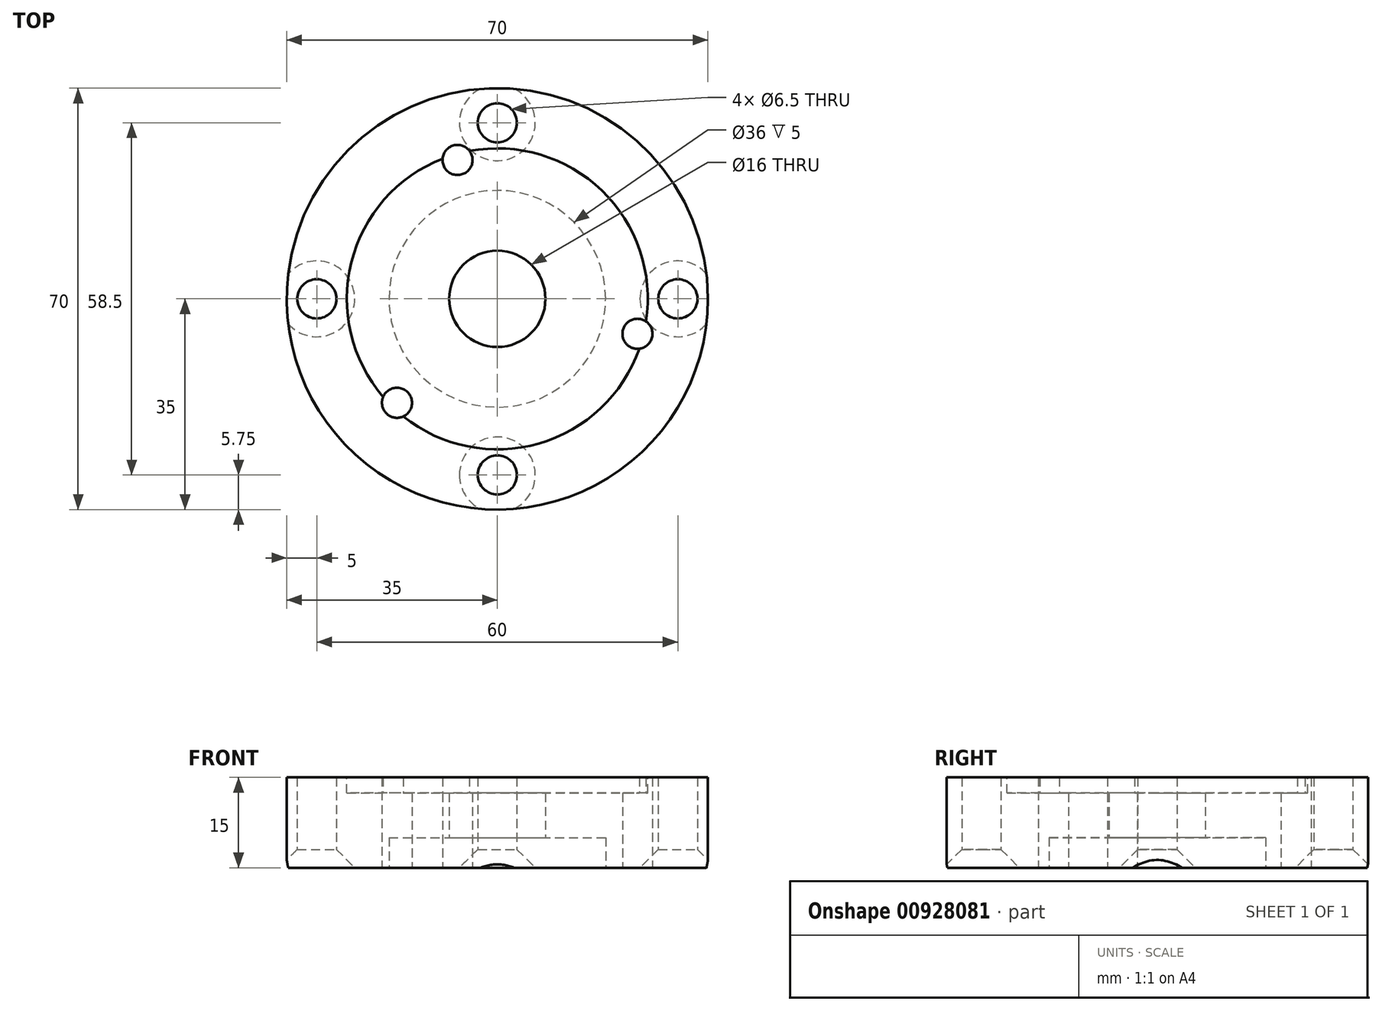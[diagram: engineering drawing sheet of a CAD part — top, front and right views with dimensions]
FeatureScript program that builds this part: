
annotation { "Feature Type Name" : "Feature", "Feature Type Description" : "" }
export const myFeature = defineFeature(function(context is Context, id is Id, definition is map)
    precondition{}
    {
        {
            var Q0;
            Q0=qCreatedBy(makeId("Top.planeOp"),FACE);
            var sketch = newSketch(context, id + "F0", { "sketchPlane" : qUnion([Q0])});
            skCircle(sketch, "E0", {"center": v(0, 0) * mm, "radius": 35 * mm});
            skSolve(sketch);
        }
        {
            var Q0;
            Q0=makeQuery(id+"F0.imprint","IMPRINT",FACE,{"disambiguationData":[TD([[makeQuery(id+"F0.imprint","IMPRINT",EDGE,{"derivedFrom":sQuery(id+"F0.wireOp",EDGE,"E0")}),1.0]])]});
            extrude(context, id + "F1", {"entities" : qUnion([Q0]), "depth" : 15 * mm, "offsetDistance" : 25 * mm});
        }
        {
            var Q0;
            Q0=makeQuery(id+"F1.opExtrude","CAP_FACE",FACE,{"disambiguationData":[OSD([sQuery(id+"F0.wireOp",EDGE,"E0")])],"isStart":false});
            var sketch = newSketch(context, id + "F2", { "sketchPlane" : qUnion([Q0])});
            skCircle(sketch, "E1", {"center": v(0, 0) * mm, "radius": 25 * mm});
            skSolve(sketch);
        }
        {
            var Q0;
            Q0=makeQuery(id+"F2.imprint","IMPRINT",FACE,{"disambiguationData":[TD([[makeQuery(id+"F2.imprint","IMPRINT",EDGE,{"derivedFrom":sQuery(id+"F2.wireOp",EDGE,"E1")}),1.0]])]});
            extrude(context, id + "F3", {"entities" : qUnion([Q0]), "operationType" : NewBodyOperationType.REMOVE, "oppositeDirection" : true, "depth" : 2.6 * mm, "offsetDistance" : 25 * mm});
        }
        {
            var Q0;
            Q0=makeQuery(id+"F1.opExtrude","CAP_FACE",FACE,{"disambiguationData":[OSD([sQuery(id+"F0.wireOp",EDGE,"E0")])],"isStart":true});
            var sketch = newSketch(context, id + "F4", { "sketchPlane" : qUnion([Q0])});
            skCircle(sketch, "E2", {"center": v(0, 0) * mm, "radius": 18 * mm});
            skCircle(sketch, "E3", {"center": v(0, 0) * mm, "radius": 29.25 * mm, "construction": true});
            skCircle(sketch, "E4", {"center": v(0, 0) * mm, "radius": 30 * mm, "construction": true});
            skPoint(sketch, "E5", {"position": v(0, -29.25) * mm});
            skPoint(sketch, "E6", {"position": v(0, 29.25) * mm});
            skPoint(sketch, "E7", {"position": v(30, 0) * mm});
            skPoint(sketch, "E8", {"position": v(-30, 0) * mm});
            skCircle(sketch, "E9", {"center": v(0, 0) * mm, "radius": 24 * mm, "construction": true});
            skPoint(sketch, "E10", {"position": v(-6.62, -23.07) * mm});
            skPoint(sketch, "E11.1.0", {"position": v(23.29, 5.8) * mm});
            skPoint(sketch, "E11.2.0", {"position": v(-16.67, 17.26) * mm});
            skSolve(sketch);
        }
        {
            var Q0;
            Q0=makeQuery(id+"F4.imprint","IMPRINT",FACE,{"disambiguationData":[TD([[makeQuery(id+"F4.imprint","IMPRINT",EDGE,{"derivedFrom":sQuery(id+"F4.wireOp",EDGE,"E2")}),1.0]])]});
            extrude(context, id + "F5", {"entities" : qUnion([Q0]), "operationType" : NewBodyOperationType.REMOVE, "oppositeDirection" : true, "depth" : 5 * mm, "offsetDistance" : 25 * mm});
        }
        {
            var Q0;
            Q0=sQuery(id+"F4.wireOp",VERTEX,"E10");
            var Q1;
            Q1=sQuery(id+"F4.wireOp",VERTEX,"E11.2.0");
            var Q2;
            Q2=sQuery(id+"F4.wireOp",VERTEX,"E11.1.0");
            var Q3;
            Q3=makeQuery(id+"F1.opExtrude","SWEPT_BODY",BODY,{"disambiguationData":[OSD([sQuery(id+"F0.wireOp",EDGE,"E0")])]});
            hole(context, id + "F6", {"style" : HoleStyle.SIMPLE, "endStyle" : HoleEndStyle.THROUGH, "standardTappedOrClearance" : lookupTablePath({ "standard" : "ISO", "engagement" : "75%", "pitch" : "1 mm", "size" : "M6", "type" : "Tapped" }), "standardBlindInLast" : lookupTablePath({ "standard" : "ISO", "engagement" : "75%", "pitch" : "1 mm", "size" : "M6", "type" : "Tapped" }), "holeDiameter" : 5 * mm, "majorDiameter" : 6 * mm, "showTappedDepth" : true, "isTappedThrough" : true, "tappedDepth" : 12 * mm, "tapClearance" : 3, "startFromSketch" : true, "locations" : qUnion([Q0, Q1, Q2]), "scope" : qUnion([Q3])});
        }
        {
            var Q0;
            Q0=sQuery(id+"F4.wireOp",VERTEX,"E7");
            var Q1;
            Q1=sQuery(id+"F4.wireOp",VERTEX,"E8");
            var Q2;
            Q2=sQuery(id+"F4.wireOp",VERTEX,"E5");
            var Q3;
            Q3=sQuery(id+"F4.wireOp",VERTEX,"E6");
            var Q4;
            Q4=makeQuery(id+"F1.opExtrude","SWEPT_BODY",BODY,{"disambiguationData":[OSD([sQuery(id+"F0.wireOp",EDGE,"E0")])]});
            hole(context, id + "F7", {"style" : HoleStyle.C_SINK, "endStyle" : HoleEndStyle.THROUGH, "standardTappedOrClearance" : lookupTablePath({ "standard" : "ISO", "size" : "6.5", "type" : "Drilled" }), "standardBlindInLast" : lookupTablePath({ "standard" : "ISO", "size" : "6.5", "type" : "Drilled" }), "holeDiameter" : 6.5 * mm, "cSinkDiameter" : 12.6 * mm, "cSinkAngle" : 90 * degree, "majorDiameter" : 6 * mm, "isTappedThrough" : true, "tappedDepth" : 12 * mm, "tapClearance" : 3, "startFromSketch" : true, "locations" : qUnion([Q0, Q1, Q2, Q3]), "scope" : qUnion([Q4])});
        }
        {
            var Q0;
            Q0=sQuery(id+"F4.wireOp",VERTEX,"E2.center");
            var Q1;
            Q1=makeQuery(id+"F1.opExtrude","SWEPT_BODY",BODY,{"disambiguationData":[OSD([sQuery(id+"F0.wireOp",EDGE,"E0")])]});
            hole(context, id + "F8", {"style" : HoleStyle.SIMPLE, "endStyle" : HoleEndStyle.THROUGH, "standardTappedOrClearance" : lookupTablePath({ "standard" : "ISO", "size" : "16", "type" : "Drilled" }), "standardBlindInLast" : lookupTablePath({ "standard" : "ISO", "size" : "16", "type" : "Drilled" }), "holeDiameter" : 16 * mm, "majorDiameter" : 6 * mm, "isTappedThrough" : true, "tappedDepth" : 12 * mm, "tapClearance" : 3, "startFromSketch" : true, "locations" : qUnion([Q0]), "scope" : qUnion([Q1])});
        }
    });
